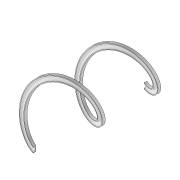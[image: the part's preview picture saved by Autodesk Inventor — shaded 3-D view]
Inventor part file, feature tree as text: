
AUTODESK INVENTOR PART (.ipt)
format: ipt  version: 2020 (Build 240168000, 168)  size: 163,328 bytes
history: native  units: mm
features: other x1, sketch x1
ambient origin geometry x8: Origin, YZ Plane, XZ Plane, XY Plane, X Axis, Y Axis, Z Axis, Center Point
bodies: Volumenkörper1 (feature_tree)
feature tree (2):
  other  "Spirale1"
  sketch  "Skizze1"  dims[d0=200.0mm d1=10.0mm d2=20.0mm d3=0.0mm d4=90.0deg d5=90.0deg d6=0.0mm d7=0.0mm d8=7.5mm d9=20.0mm d10=10.0mm]
